# Revit family: NBS_CordekLtd_DschrgeAndVntltngStackTrmntns_GasVentingBollard-026
name_source: partatom
category: Specialty Equipment
revit_build: Autodesk Revit 2014 (Build: 20131024_2115(x64)
units: mm (PartAtom-declared; Revit-internal decimal feet)

## types (1)
- GasVentingBollard-026
    Accessories = Horizontal extension sleeve
    Arrangement = Bollard with vents
    AssetType = Fixed
    BIMObjectName = NBS_CordekLtd_DischargeAndVentilatingStackTerminations_GasVentingBollard-026
    BollardMaterial = NBS_Concept
    Category = Pr_65_52_61_23:Discharge and ventilating stack terminations
    Color = Natural
    Description = Stainless steel gas venting bollard
    DurationUnit = year
    Features = Can be positioned at large centres due to high level of free air flow, high quality, robust construction, elevated vent position to avoid potential for water and/or debris ingress
    FreeAirFlow = 25000 mm²
    Height = 1100 mm  [stored 3.60892 ft]
    IfcExportAs = IfcStackTerminalType
    IfcExportType = NOTDEFINED
    Length = 110 mm  [stored 0.360892 ft]
    ManufacturerName = Cordek Ltd
    ManufacturerURL = www.cordek.com
    Material = Stainless steel
    ModelNumber = CGV-026
    ModelReference = Gas Venting Bollard - 026
    NBSCertification = http://www.nationalbimlibrary.com
    NBSDescription = Discharge and ventilating stack terminations
    NBSReference = 90-10-60/437
    Name = DischargeAndVentilatingStackTerminations_GasVentingBollard-026_CordekLtd
    NominalHeight = 1100 mm  [stored 3.60892 ft]
    NominalLength = 110 mm  [stored 0.360892 ft]
    NominalWidth = 110 mm  [stored 0.360892 ft]
    ProductInformation = www.cordek.com/uploads/data_sheets/M-DS16_gas_venting_bollard_data_sheet_v2_cordek.pdf
    Shape = Circular
    Size = 110 x 110 x 1100 mm
    Uniclass2 = 90-62-24/422
    Uniclass2015Description = Discharge and ventilating stack terminations
    Uniclass2015Reference = Pr_65_52_61_23
    Uniclass2015Version = Products v1.1
    Version = 1
    WarrantyDurationUnit = year
    Weight = 7.920 kg
    Width = 110 mm  [stored 0.360892 ft]

note: [stored X ft] marks values corroborated as IEEE doubles in the binary element streams (Revit-internal decimal feet)

## geometry (parser evidence)
native form markers: Sweep x1
no freeform markers — native parametric forms only
